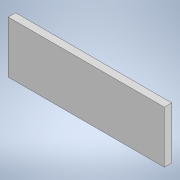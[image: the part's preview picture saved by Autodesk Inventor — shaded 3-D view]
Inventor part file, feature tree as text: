
AUTODESK INVENTOR PART (.ipt)
format: ipt  version: 2020.1 (Build 241239000, 239)  size: 88,064 bytes
history: native  units: in
note: dims shown in document units (in); Inventor stores cm internally (conversion verified against a paired STEP export)
features: extrude x1, sketch x1
ambient origin geometry x8: Origin, YZ Plane, XZ Plane, XY Plane, X Axis, Y Axis, Z Axis, Center Point
bodies: Solid1 (feature_tree)
feature tree (2):
  extrude  "Extrusion1"  Depth=252.0in
  sketch  "Sketch1"  dims[d0=84.0in d1=252.0in d2=12.0in d3=0.0in]
